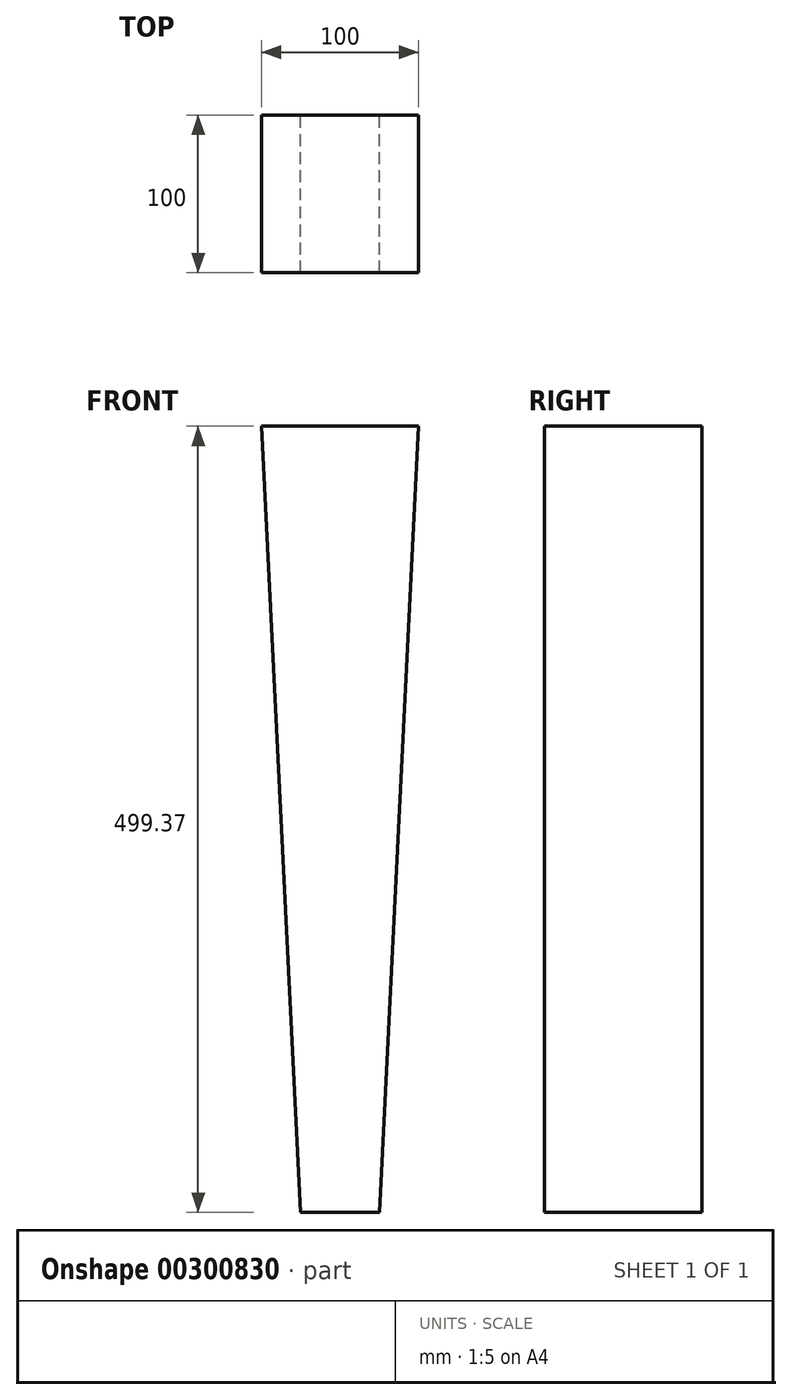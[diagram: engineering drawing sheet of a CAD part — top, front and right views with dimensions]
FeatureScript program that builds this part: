
annotation { "Feature Type Name" : "Feature", "Feature Type Description" : "" }
export const myFeature = defineFeature(function(context is Context, id is Id, definition is map)
    precondition{}
    {
        {
            var Q0;
            Q0=qCreatedBy(makeId("Front.planeOp"),FACE);
            var sketch = newSketch(context, id + "F0", { "sketchPlane" : qUnion([Q0])});
            skLineSegment(sketch, "E0", {"start": v(0, 0) * mm, "end": v(50, 0) * mm});
            skLineSegment(sketch, "E1", {"start": v(50, 0) * mm, "end": v(25, -499.37) * mm});
            skLineSegment(sketch, "E2", {"start": v(25, -499.37) * mm, "end": v(0, -499.37) * mm});
            skLineSegment(sketch, "E3", {"start": v(0, 0) * mm, "end": v(0, -499.37) * mm});
            skPoint(sketch, "E4", {"position": v(0, -249.69) * mm});
            skLineSegment(sketch, "E5", {"start": v(0, 0) * mm, "end": v(-50, 0) * mm});
            skLineSegment(sketch, "E6", {"start": v(-50, 0) * mm, "end": v(-25, -499.37) * mm});
            skLineSegment(sketch, "E7", {"start": v(-25, -499.37) * mm, "end": v(0, -499.37) * mm});
            skSolve(sketch);
        }
        {
            var Q0;
            Q0=makeQuery(id+"F0.imprint","IMPRINT",FACE,{"disambiguationData":[TD([[makeQuery(id+"F0.imprint","IMPRINT",EDGE,{"derivedFrom":sQuery(id+"F0.wireOp",EDGE,"E3")}),-1.0]])]});
            var Q1;
            Q1=makeQuery(id+"F0.imprint","IMPRINT",FACE,{"disambiguationData":[TD([[makeQuery(id+"F0.imprint","IMPRINT",EDGE,{"derivedFrom":sQuery(id+"F0.wireOp",EDGE,"E0")}),-1.0]])]});
            extrude(context, id + "F1", {"entities" : qUnion([Q0, Q1]), "depth" : 100 * mm});
        }
    });
